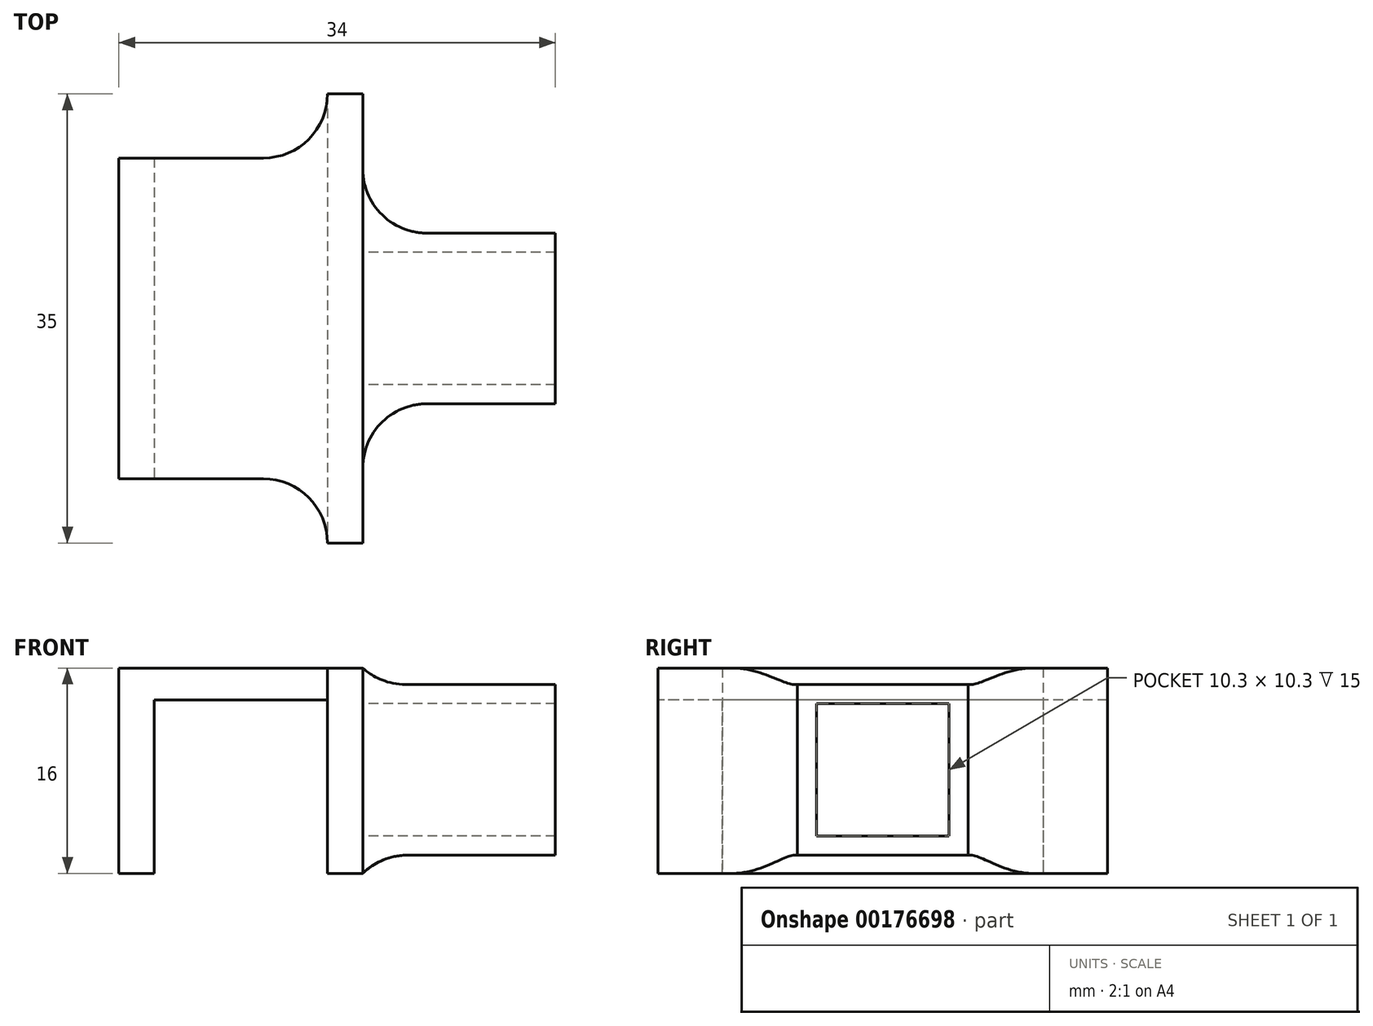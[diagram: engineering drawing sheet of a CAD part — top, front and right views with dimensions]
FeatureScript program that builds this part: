
annotation { "Feature Type Name" : "Feature", "Feature Type Description" : "" }
export const myFeature = defineFeature(function(context is Context, id is Id, definition is map)
    precondition{}
    {
        {
            var Q0;
            Q0=qCreatedBy(makeId("Top.planeOp"),FACE);
            var sketch = newSketch(context, id + "F0", { "sketchPlane" : qUnion([Q0])});
            skLineSegment(sketch, "E0.bottom", {"start": v(-9.5, 12.5) * mm, "end": v(9.5, 12.5) * mm});
            skLineSegment(sketch, "E0.top", {"start": v(-9.5, -12.5) * mm, "end": v(9.5, -12.5) * mm});
            skLineSegment(sketch, "E0.left", {"start": v(-9.5, 12.5) * mm, "end": v(-9.5, -12.5) * mm});
            skLineSegment(sketch, "E0.right", {"start": v(9.5, 12.5) * mm, "end": v(9.5, -12.5) * mm});
            skPoint(sketch, "E0.middle", {"position": v(0, 0) * mm});
            skSolve(sketch);
        }
        {
            var Q0;
            Q0=qSketchRegion(id+"F0",true);
            extrude(context, id + "F1", {"entities" : qUnion([Q0]), "depth" : 16 * mm});
        }
        {
            var Q0;
            Q0=makeQuery(id+"F1.opExtrude","SWEPT_FACE",FACE,{"disambiguationData":[OSD([sQuery(id+"F0.wireOp",EDGE,"E0.top")])]});
            var sketch = newSketch(context, id + "F2", { "sketchPlane" : qUnion([Q0])});
            skLineSegment(sketch, "E1.bottom", {"start": v(-6.75, 0) * mm, "end": v(6.75, 0) * mm});
            skLineSegment(sketch, "E1.top", {"start": v(-6.75, 13.5) * mm, "end": v(6.75, 13.5) * mm});
            skLineSegment(sketch, "E1.left", {"start": v(-6.75, 0) * mm, "end": v(-6.75, 13.5) * mm});
            skLineSegment(sketch, "E1.right", {"start": v(6.75, 0) * mm, "end": v(6.75, 13.5) * mm});
            skSolve(sketch);
        }
        {
            var Q0;
            Q0=makeQuery(id+"F2.imprint","IMPRINT",FACE,{"disambiguationData":[TD([[makeQuery(id+"F2.imprint","IMPRINT",EDGE,{"derivedFrom":sQuery(id+"F2.wireOp",EDGE,"E1.bottom")}),1.0]])]});
            extrude(context, id + "F3", {"entities" : qUnion([Q0]), "operationType" : NewBodyOperationType.REMOVE, "oppositeDirection" : true, "depth" : 50 * mm});
        }
        {
            var Q0;
            Q0=makeQuery(id+"F1.opExtrude","SWEPT_FACE",FACE,{"disambiguationData":[OSD([sQuery(id+"F0.wireOp",EDGE,"E0.right")])]});
            var sketch = newSketch(context, id + "F4", { "sketchPlane" : qUnion([Q0])});
            skLineSegment(sketch, "E2.bottom", {"start": v(-17.5, 16) * mm, "end": v(17.5, 16) * mm});
            skLineSegment(sketch, "E2.top", {"start": v(-17.5, 0) * mm, "end": v(17.5, 0) * mm});
            skLineSegment(sketch, "E2.left", {"start": v(-17.5, 16) * mm, "end": v(-17.5, 0) * mm});
            skLineSegment(sketch, "E2.right", {"start": v(17.5, 16) * mm, "end": v(17.5, 0) * mm});
            skLineSegment(sketch, "E3.bottom", {"start": v(-5.15, 13.22) * mm, "end": v(5.15, 13.22) * mm});
            skLineSegment(sketch, "E3.top", {"start": v(-5.15, 2.92) * mm, "end": v(5.15, 2.92) * mm});
            skLineSegment(sketch, "E3.left", {"start": v(-5.15, 13.22) * mm, "end": v(-5.15, 2.92) * mm});
            skLineSegment(sketch, "E3.right", {"start": v(5.15, 13.22) * mm, "end": v(5.15, 2.92) * mm});
            skLineSegment(sketch, "E4.0", {"start": v(-6.65, 14.72) * mm, "end": v(6.65, 14.72) * mm});
            skLineSegment(sketch, "E4.1", {"start": v(-6.65, 14.72) * mm, "end": v(-6.65, 1.42) * mm});
            skLineSegment(sketch, "E4.2", {"start": v(-6.65, 1.42) * mm, "end": v(6.65, 1.42) * mm});
            skLineSegment(sketch, "E4.3", {"start": v(6.65, 14.72) * mm, "end": v(6.65, 1.42) * mm});
            skLineSegment(sketch, "E5", {"start": v(0, 0) * mm, "end": v(0, 16) * mm});
            skPoint(sketch, "E6", {"position": v(0, 8) * mm});
            skPoint(sketch, "E7.positionSnap0", {"position": v(0, 13.22) * mm});
            skPoint(sketch, "E8.positionSnap0", {"position": v(0, 16) * mm});
            skPoint(sketch, "E8.positionSnap1", {"position": v(17.5, 8) * mm});
            skSolve(sketch);
        }
        {
            var Q0;
            Q0=qSketchRegion(id+"F4",true);
            var Q1;
            Q1=makeQuery(id+"F4.imprint","IMPRINT",FACE,{"disambiguationData":[TD([[makeQuery(id+"F4.imprint","IMPRINT",EDGE,{"derivedFrom":sQuery(id+"F4.wireOp",EDGE,"E3.bottom")}),-1.0]])]});
            var Q2;
            Q2=makeQuery(id+"F4.imprint","IMPRINT",FACE,{"disambiguationData":[TD([[makeQuery(id+"F4.imprint","IMPRINT",EDGE,{"derivedFrom":sQuery(id+"F4.wireOp",EDGE,"E3.bottom")}),1.0]])]});
            var Q3;
            Q3=makeQuery(id+"F4.imprint","IMPRINT",FACE,{"disambiguationData":[TD([[makeQuery(id+"F4.imprint","IMPRINT",EDGE,{"derivedFrom":sQuery(id+"F4.wireOp",EDGE,"4b76e74c-1ac9-4312-af6a-232a9c3240f70.MirrorCS")}),-1.0]])]});
            var Q4;
            Q4=makeQuery(id+"F4.imprint","IMPRINT",FACE,{"disambiguationData":[TD([[makeQuery(id+"F4.imprint","IMPRINT",EDGE,{"derivedFrom":sQuery(id+"F4.wireOp",EDGE,"4b76e74c-1ac9-4312-af6a-232a9c3240f70.MirrorCS")}),1.0]])]});
            extrude(context, id + "F5", {"entities" : qUnion([Q0, Q1, Q2, Q3, Q4]), "operationType" : NewBodyOperationType.ADD, "oppositeDirection" : true, "depth" : 2.75 * mm});
        }
        {
            var Q0;
            Q0=makeQuery(id+"F4.imprint","IMPRINT",FACE,{"disambiguationData":[TD([[makeQuery(id+"F4.imprint","IMPRINT",EDGE,{"derivedFrom":sQuery(id+"F4.wireOp",EDGE,"E3.bottom")}),1.0]])]});
            var Q1;
            Q1=makeQuery(id+"F4.imprint","IMPRINT",FACE,{"disambiguationData":[TD([[makeQuery(id+"F4.imprint","IMPRINT",EDGE,{"derivedFrom":sQuery(id+"F4.wireOp",EDGE,"4b76e74c-1ac9-4312-af6a-232a9c3240f70.MirrorCS")}),-1.0]])]});
            extrude(context, id + "F6", {"entities" : qUnion([Q0, Q1]), "operationType" : NewBodyOperationType.ADD, "depth" : 15 * mm});
        }
        {
            var Q0;
            Q0=makeQuery(id+"F5.boolean.opBoolean","INTERSECT",EDGE,{"derivedFrom":[makeQuery(id+"F1.opExtrude","SWEPT_FACE",FACE,{"disambiguationData":[OSD([sQuery(id+"F0.wireOp",EDGE,"E0.bottom")])]}),makeQuery(id+"F5.opExtrude","CAP_FACE",FACE,{"disambiguationData":[OSD([sQuery(id+"F4.wireOp",EDGE,"E2.bottom"),sQuery(id+"F4.wireOp",EDGE,"E2.top"),sQuery(id+"F4.wireOp",EDGE,"E2.left"),sQuery(id+"F4.wireOp",EDGE,"E2.right")])],"isStart":false})]});
            var Q1;
            Q1=makeQuery(id+"F5.boolean.opBoolean","INTERSECT",EDGE,{"derivedFrom":[makeQuery(id+"F1.opExtrude","SWEPT_FACE",FACE,{"disambiguationData":[OSD([sQuery(id+"F0.wireOp",EDGE,"E0.top")])]}),makeQuery(id+"F5.opExtrude","CAP_FACE",FACE,{"disambiguationData":[OSD([sQuery(id+"F4.wireOp",EDGE,"E2.bottom"),sQuery(id+"F4.wireOp",EDGE,"E2.top"),sQuery(id+"F4.wireOp",EDGE,"E2.left"),sQuery(id+"F4.wireOp",EDGE,"E2.right")])],"isStart":false})]});
            var Q2;
            Q2=makeQuery(id+"F6.opExtrude","CAP_EDGE",EDGE,{"disambiguationData":[OSD([sQuery(id+"F4.wireOp",EDGE,"E4.0")])],"isStart":true});
            var Q3;
            Q3=makeQuery(id+"F6.opExtrude","CAP_EDGE",EDGE,{"disambiguationData":[OSD([sQuery(id+"F4.wireOp",EDGE,"E4.1")])],"isStart":true});
            var Q4;
            Q4=makeQuery(id+"F6.opExtrude","CAP_EDGE",EDGE,{"disambiguationData":[OSD([sQuery(id+"F4.wireOp",EDGE,"E4.3")])],"isStart":true});
            var Q5;
            Q5=makeQuery(id+"F6.opExtrude","CAP_EDGE",EDGE,{"disambiguationData":[OSD([sQuery(id+"F4.wireOp",EDGE,"E4.2")])],"isStart":true});
            fillet(context, id + "F7", {"entities" : qUnion([Q0, Q1, Q2, Q3, Q4, Q5]), "radius" : 5 * mm, "tangentPropagation" : true, "allowEdgeOverflow" : false});
        }
    });
